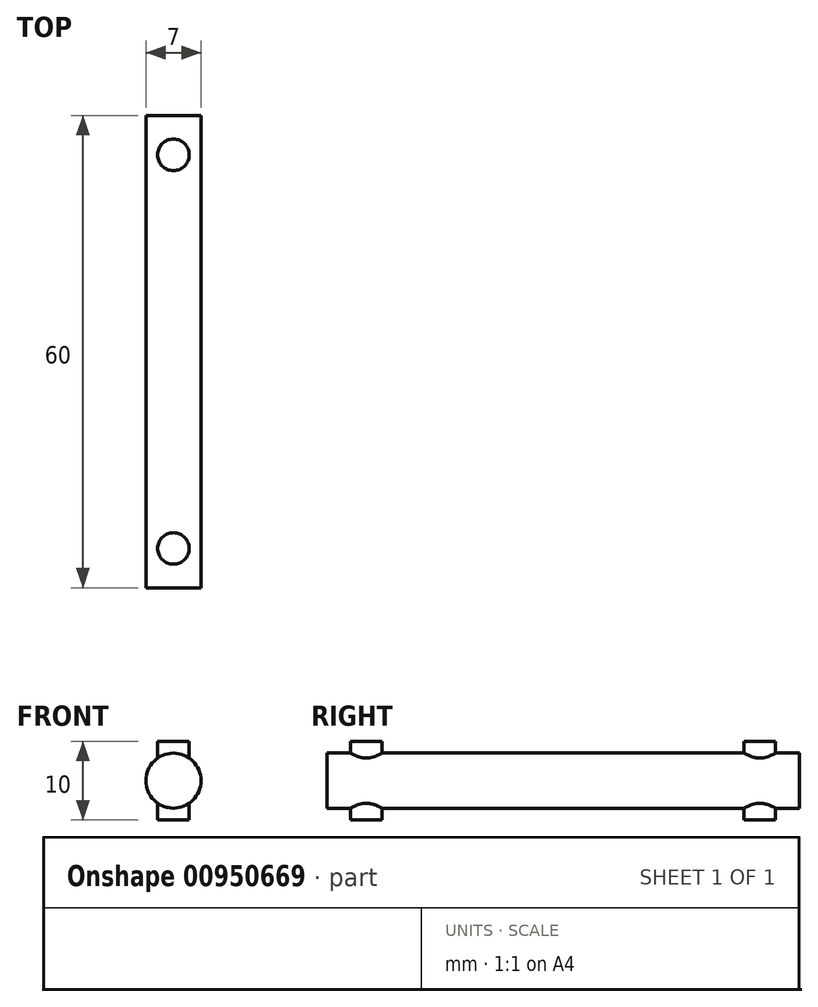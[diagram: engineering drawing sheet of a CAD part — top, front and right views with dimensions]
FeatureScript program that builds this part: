
annotation { "Feature Type Name" : "Feature", "Feature Type Description" : "" }
export const myFeature = defineFeature(function(context is Context, id is Id, definition is map)
    precondition{}
    {
        {
            var Q0;
            Q0=qCreatedBy(makeId("Front.planeOp"),FACE);
            var sketch = newSketch(context, id + "F0", { "sketchPlane" : qUnion([Q0])});
            skCircle(sketch, "E0", {"center": v(0, 0) * mm, "radius": 3.5 * mm});
            skSolve(sketch);
        }
        {
            var Q0;
            Q0=makeQuery(id+"F0.imprint","IMPRINT",FACE,{"disambiguationData":[TD([[makeQuery(id+"F0.imprint","IMPRINT",EDGE,{"derivedFrom":sQuery(id+"F0.wireOp",EDGE,"E0")}),1.0]])]});
            extrude(context, id + "F1", {"entities" : qUnion([Q0]), "depth" : 60 * mm, "offsetDistance" : 25 * mm});
        }
        {
            var Q0;
            Q0=qCreatedBy(makeId("Top.planeOp"),FACE);
            var sketch = newSketch(context, id + "F2", { "sketchPlane" : qUnion([Q0])});
            skLineSegment(sketch, "E1", {"start": v(0, 7.9) * mm, "end": v(0, -62.1) * mm});
            skPoint(sketch, "E2", {"position": v(0, -55) * mm});
            skPoint(sketch, "E3", {"position": v(0, -5) * mm});
            skCircle(sketch, "E4", {"center": v(0, -5) * mm, "radius": 2 * mm});
            skCircle(sketch, "E5", {"center": v(0, -55) * mm, "radius": 2 * mm});
            skSolve(sketch);
        }
        {
            var Q0;
            {var subQ0=sQuery(id+"F2.wireOp",EDGE,"E4");var subQ1=sQuery(id+"F2.wireOp",EDGE,"E1");var subQ2=makeQuery(id+"F2.imprint","INTERSECT",VERTEX,{"disambiguationData":[OD(0.0)],"derivedFrom":[subQ1,subQ0]});Q0=makeQuery(id+"F2.imprint","IMPRINT",FACE,{"disambiguationData":[TD([[makeQuery(id+"F2.imprint","IMPRINT",EDGE,{"disambiguationData":[TD([[subQ2,1.0]])],"derivedFrom":subQ1}),-1.0]])]});}
            var Q1;
            {var subQ0=sQuery(id+"F2.wireOp",EDGE,"E4");var subQ1=sQuery(id+"F2.wireOp",EDGE,"E1");var subQ2=makeQuery(id+"F2.imprint","INTERSECT",VERTEX,{"disambiguationData":[OD(0.0)],"derivedFrom":[subQ1,subQ0]});Q1=makeQuery(id+"F2.imprint","IMPRINT",FACE,{"disambiguationData":[TD([[makeQuery(id+"F2.imprint","IMPRINT",EDGE,{"disambiguationData":[TD([[subQ2,1.0]])],"derivedFrom":subQ1}),1.0]])]});}
            var Q2;
            {var subQ0=sQuery(id+"F2.wireOp",EDGE,"E5");var subQ1=sQuery(id+"F2.wireOp",EDGE,"E1");var subQ2=makeQuery(id+"F2.imprint","INTERSECT",VERTEX,{"disambiguationData":[OD(0.0)],"derivedFrom":[subQ1,subQ0]});Q2=makeQuery(id+"F2.imprint","IMPRINT",FACE,{"disambiguationData":[TD([[makeQuery(id+"F2.imprint","IMPRINT",EDGE,{"disambiguationData":[TD([[subQ2,1.0]])],"derivedFrom":subQ1}),1.0]])]});}
            var Q3;
            {var subQ0=sQuery(id+"F2.wireOp",EDGE,"E5");var subQ1=sQuery(id+"F2.wireOp",EDGE,"E1");var subQ2=makeQuery(id+"F2.imprint","INTERSECT",VERTEX,{"disambiguationData":[OD(0.0)],"derivedFrom":[subQ1,subQ0]});Q3=makeQuery(id+"F2.imprint","IMPRINT",FACE,{"disambiguationData":[TD([[makeQuery(id+"F2.imprint","IMPRINT",EDGE,{"disambiguationData":[TD([[subQ2,1.0]])],"derivedFrom":subQ1}),-1.0]])]});}
            extrude(context, id + "F3", {"entities" : qUnion([Q0, Q1, Q2, Q3]), "operationType" : NewBodyOperationType.ADD, "endBound" : BoundingType.SYMMETRIC, "depth" : 10 * mm, "offsetDistance" : 25 * mm});
        }
    });
